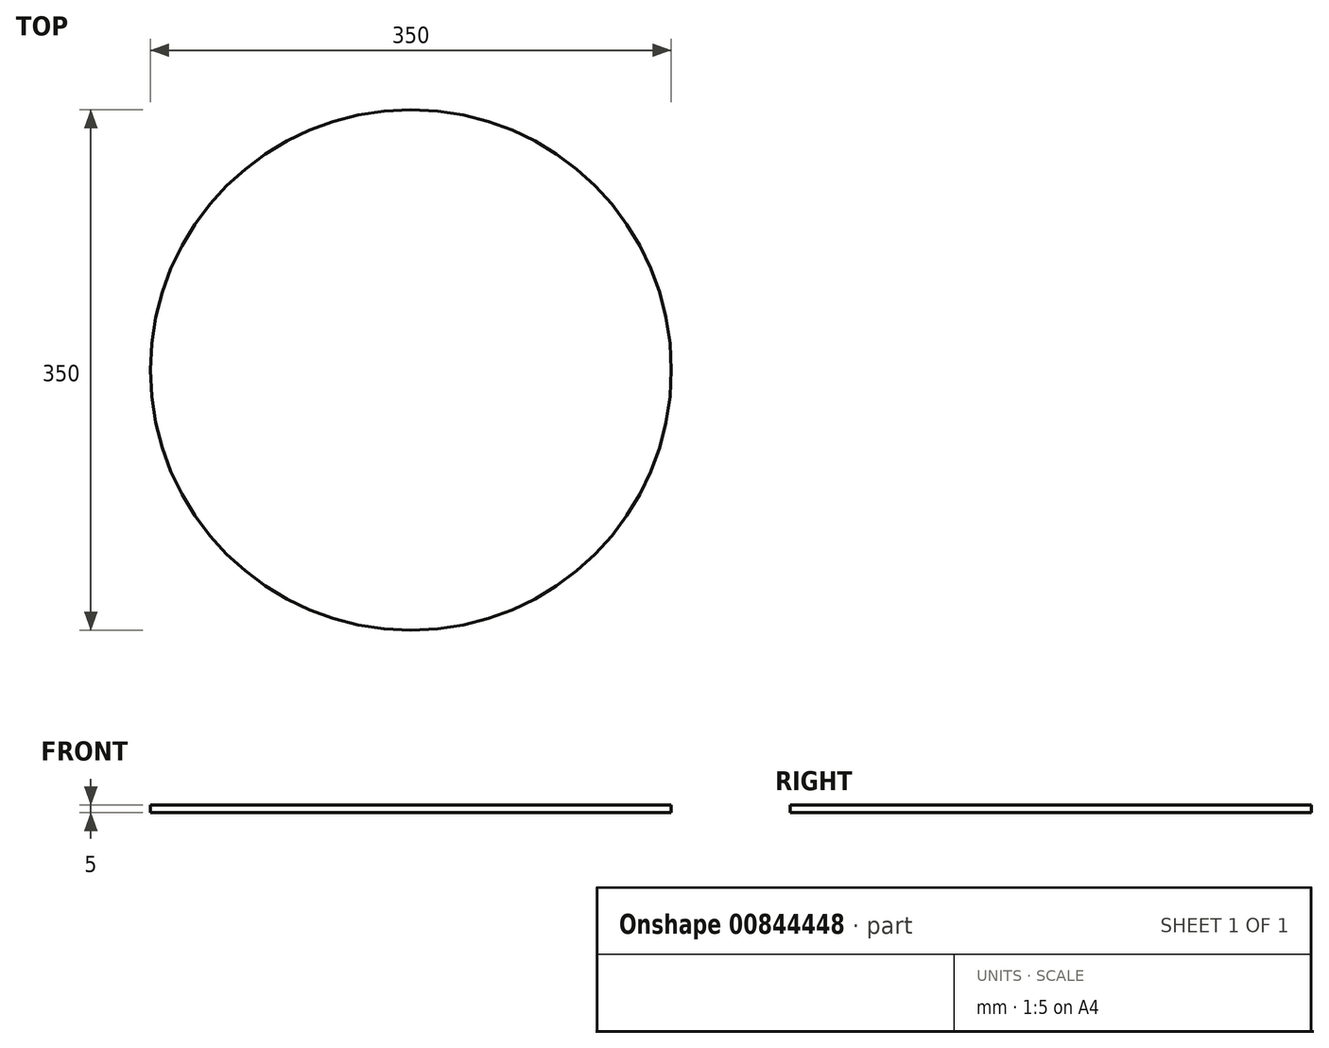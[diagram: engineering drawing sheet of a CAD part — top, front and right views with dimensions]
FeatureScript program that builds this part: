
annotation { "Feature Type Name" : "Feature", "Feature Type Description" : "" }
export const myFeature = defineFeature(function(context is Context, id is Id, definition is map)
    precondition{}
    {
        {
            var Q0;
            Q0=qCreatedBy(makeId("Top.planeOp"),FACE);
            var sketch = newSketch(context, id + "F0", { "sketchPlane" : qUnion([Q0])});
            skCircle(sketch, "E0", {"center": v(0, 0) * mm, "radius": 175 * mm});
            skSolve(sketch);
        }
        {
            var Q0;
            Q0 = qSketchRegion(id + "F0", true);
            extrude(context, id + "F1", {"entities" : qUnion([Q0]), "depth" : 5 * mm, "offsetDistance" : 25 * mm});
        }
    });
